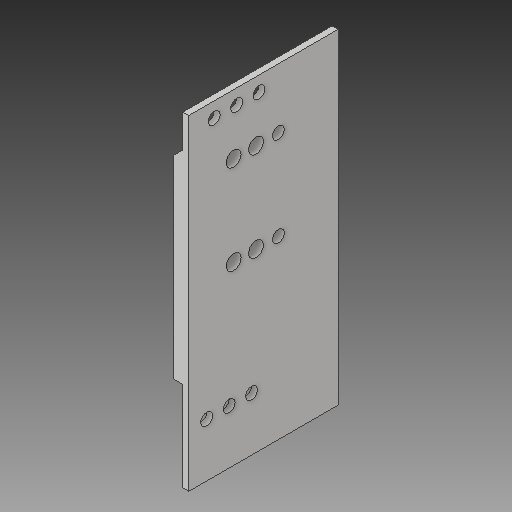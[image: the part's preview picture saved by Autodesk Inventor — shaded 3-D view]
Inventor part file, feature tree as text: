
AUTODESK INVENTOR PART (.ipt)
format: ipt  version: 2018 (Build 220112000, 112)  size: 148,480 bytes
history: native  units: mm
features: extrude x3, sketch x3
ambient origin geometry x8: Origin, YZ Plane, XZ Plane, XY Plane, X Axis, Y Axis, Z Axis, Center Point
bodies: Solid1 (feature_tree)
feature tree (6):
  extrude  "Extrusion1"  Depth=218.0mm
  extrude  "Extrusion2"  Depth=4.0mm
  extrude  "Extrusion3"  TaperAngle=135.0deg  [1 undecoded]
  sketch  "Sketch1"  dims[d0=100.0mm d1=218.0mm]
  sketch  "Sketch2"  dims[d2=10.0mm d3=0.0mm d5=4.0mm]
  sketch  "Sketch3"  dims[d6=22.0mm d7=135.0deg d8=60.0mm d10=4.0mm d11=10.0mm d12=0.0mm d13=8.0mm d14=8.0mm d15=17.0mm d16=15.0mm d17=15.0mm d18=10.0mm d19=12.0mm d20=15.0mm d21=15.0mm d22=36.0mm d23=10.0mm d24=8.0mm d25=40.0mm d26=30.0mm d27=15.0mm d28=15.0mm d29=60.0mm d30=15.0mm d31=15.0mm d32=10.0mm d33=0.0mm]
note: 1 required parameter value undecoded (feature->parameter linkage not recoverable at this tier; creation-order binding heuristic only, values carry confidence <= 0.55)
